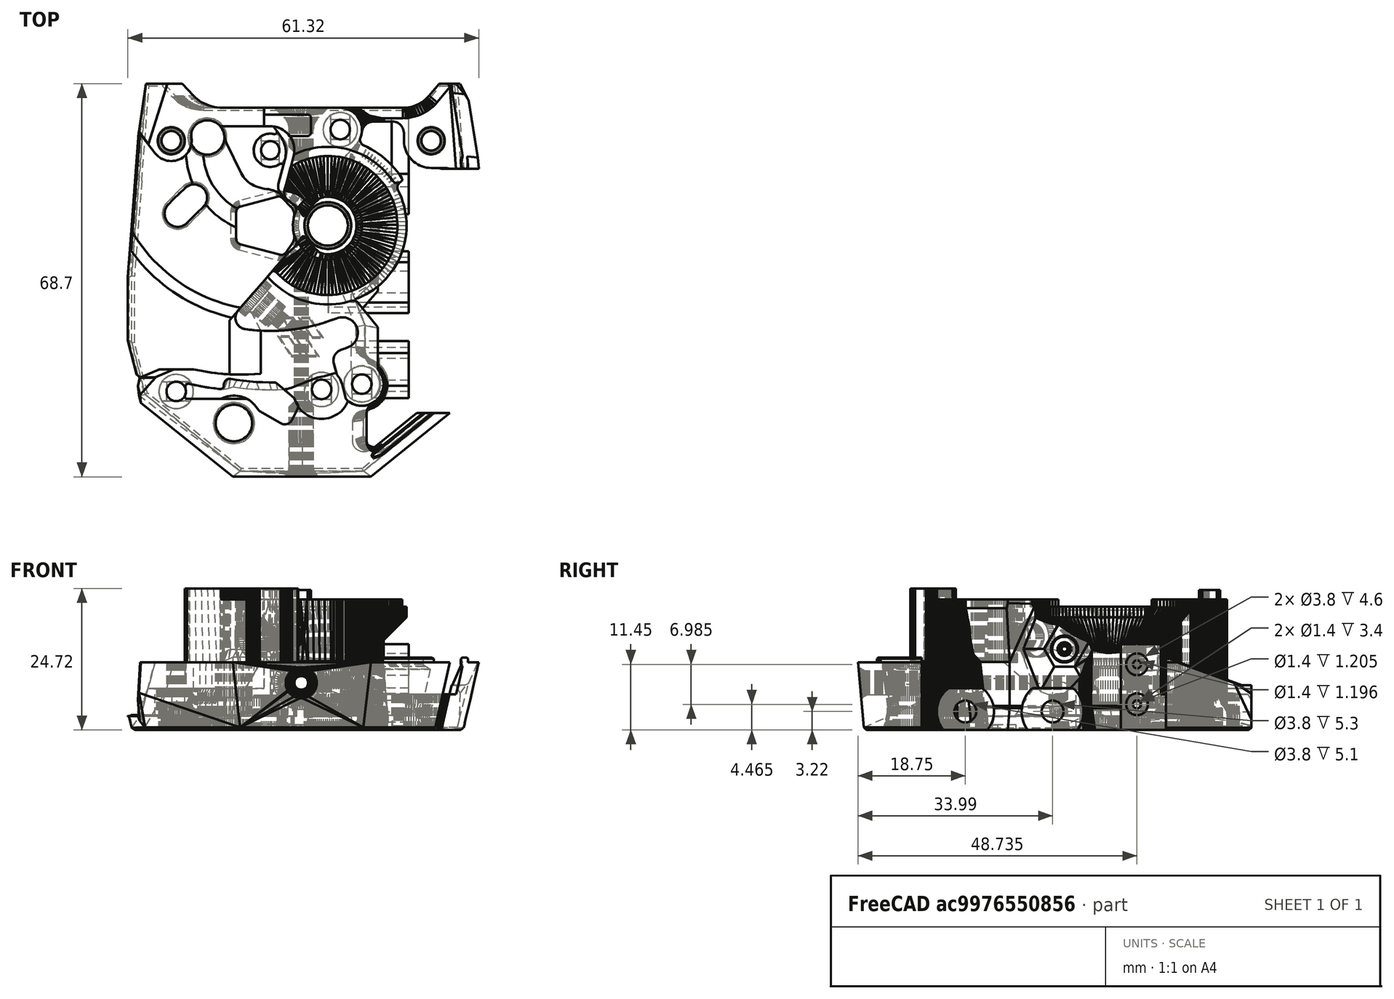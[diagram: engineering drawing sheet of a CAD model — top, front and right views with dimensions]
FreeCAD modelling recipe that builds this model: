
FCSTD DOCUMENT  (FreeCAD 0.19R24366 (Git))
Label: sb-mod2
License: All rights reserved
LicenseURL: http://en.wikipedia.org/wiki/All_rights_reserved
objects: Part::Cylinder×17, Part::Box×6, Part::MultiFuse×5, Part::Cut×3, Mesh::Feature×1, Part::Feature×1, Part::Compound×1
note: 33 computed .brp shape members not serialized (recipe doc carries the construction recipe); baked Part::Feature solids carry a one-line shape summary decoded from their .brp

FEATURE [Mesh::Feature] motor_plate
  Placement = pos=(-1.79,11.67,30.614) rot=(0,1,0;3.14159rad)
FEATURE [Part::Cylinder] Cylinder002
  Angle = 360
  AttacherType = Attacher::AttachEngine3D
  Height = 12
  Placement = pos=(9.55,-17.66,-3) rot=(0,0,1;0rad)
  Radius = 3.2
FEATURE [Part::Cylinder] Cylinder003
  Angle = 360
  AttacherType = Attacher::AttachEngine3D
  Height = 14
  Placement = pos=(17.64,0.14,3.22) rot=(0,-1,0;1.5708rad)
  Radius = 5.4
FEATURE [Part::Box] Box001  label="Cube001"
  AttacherType = Attacher::AttachEngine3D
  Height = 15
  Length = 10.6
  Placement = pos=(7.04,12.06,0) rot=(0,0,1;0rad)
  Width = 7
FEATURE [Part::Cylinder] Cylinder004
  Angle = 360
  AttacherType = Attacher::AttachEngine3D
  Height = 11.5
  Placement = pos=(3.62,10.05,0) rot=(0,0,1;0rad)
  Radius = 5.8
FEATURE [Part::Cylinder] Cylinder005
  Angle = 360
  AttacherType = Attacher::AttachEngine3D
  Height = 5
  Placement = pos=(3.62,10.05,11) rot=(0,0,1;0rad)
  Radius = 7
FEATURE [Part::Box] Box002  label="Cube002"
  AttacherType = Attacher::AttachEngine3D
  Height = 10
  Length = 10
  Placement = pos=(7.64,-21.3,7.32) rot=(0,0,1;0rad)
  Width = 30
FEATURE [Part::Box] Box003  label="Cube003"
  AttacherType = Attacher::AttachEngine3D
  Height = 10
  Length = 15
  Placement = pos=(2.64,-21.3,-9.985) rot=(0,0,1;0rad)
  Width = 30
FEATURE [Part::Cylinder] Cylinder001
  Angle = 360
  AttacherType = Attacher::AttachEngine3D
  Height = 10
  Placement = pos=(17.64,-15.1,3.22) rot=(0,-1,0;1.5708rad)
  Radius = 5
FEATURE [Part::Cylinder] Cylinder006
  Angle = 360
  AttacherType = Attacher::AttachEngine3D
  Height = 4.6
  Placement = pos=(17.64,14.885,4.465) rot=(0,-1,0;1.5708rad)
  Radius = 1.9
FEATURE [Part::Cylinder] Cylinder007
  Angle = 360
  AttacherType = Attacher::AttachEngine3D
  Height = 4.6
  Placement = pos=(17.64,14.885,11.45) rot=(0,-1,0;1.5708rad)
  Radius = 1.9
FEATURE [Part::Cylinder] Cylinder008
  Angle = 360
  AttacherType = Attacher::AttachEngine3D
  Height = 5.3
  Placement = pos=(17.64,0.14,3.22) rot=(0,-1,0;1.5708rad)
  Radius = 1.9
FEATURE [Part::Box] Box004  label="Cube004"
  AttacherType = Attacher::AttachEngine3D
  Height = 13
  Length = 14
  Placement = pos=(17.64,-22.73,0) rot=(0,0,1;0rad)
  Width = 42.7
FEATURE [Part::Feature] main_body001_solid  label="main_body001 (Solid)"
  shape: bbox 62.85 x 68.69 x 24.7 mm, 21214 faces (baked)
FEATURE [Part::Cylinder] Cylinder009
  Angle = 360
  AttacherType = Attacher::AttachEngine3D
  Height = 8
  Placement = pos=(17.64,14.885,4.465) rot=(0,-1,0;1.5708rad)
  Radius = 0.7
FEATURE [Part::Cylinder] Cylinder010
  Angle = 360
  AttacherType = Attacher::AttachEngine3D
  Height = 8
  Placement = pos=(17.64,14.885,11.45) rot=(0,-1,0;1.5708rad)
  Radius = 0.7
FEATURE [Part::Cylinder] Cylinder
  Angle = 360
  AttacherType = Attacher::AttachEngine3D
  Height = 5.1
  Placement = pos=(17.64,-15.1,3.22) rot=(0,-1,0;1.5708rad)
  Radius = 1.9
FEATURE [Part::MultiFuse] Fusion003
  Shapes = -> [Cylinder,Cylinder006,Cylinder007,Cylinder008,Box004,Cylinder009,Cylinder010]
FEATURE [Part::MultiFuse] Fusion004
  Shapes = -> [Box003,Cylinder002,Cylinder004,Cylinder005,Box002]
FEATURE [Part::MultiFuse] Fusion
  Shapes = -> [Cylinder003,Box001,Cylinder001]
FEATURE [Part::Cut] Cut
  Base = -> Fusion
  Tool = -> Fusion004
FEATURE [Part::Cylinder] Cylinder011
  Angle = 360
  AttacherType = Attacher::AttachEngine3D
  Height = 5.1
  Placement = pos=(17.64,-15.1,3.22) rot=(0,-1,0;1.5708rad)
  Radius = 1.9
FEATURE [Part::Cylinder] Cylinder012
  Angle = 360
  AttacherType = Attacher::AttachEngine3D
  Height = 4.6
  Placement = pos=(17.64,14.885,4.465) rot=(0,-1,0;1.5708rad)
  Radius = 1.9
FEATURE [Part::Cylinder] Cylinder013
  Angle = 360
  AttacherType = Attacher::AttachEngine3D
  Height = 4.6
  Placement = pos=(17.64,14.885,11.45) rot=(0,-1,0;1.5708rad)
  Radius = 1.9
FEATURE [Part::Cylinder] Cylinder014
  Angle = 360
  AttacherType = Attacher::AttachEngine3D
  Height = 5.3
  Placement = pos=(17.64,0.14,3.22) rot=(0,-1,0;1.5708rad)
  Radius = 1.9
FEATURE [Part::Box] Box005  label="Cube005"
  AttacherType = Attacher::AttachEngine3D
  Height = 13
  Length = 14
  Placement = pos=(17.64,-22.73,0) rot=(0,0,1;0rad)
  Width = 42.7
FEATURE [Part::Cylinder] Cylinder015
  Angle = 360
  AttacherType = Attacher::AttachEngine3D
  Height = 8
  Placement = pos=(17.64,14.885,4.465) rot=(0,-1,0;1.5708rad)
  Radius = 0.7
FEATURE [Part::Cylinder] Cylinder016
  Angle = 360
  AttacherType = Attacher::AttachEngine3D
  Height = 8
  Placement = pos=(17.64,14.885,11.45) rot=(0,-1,0;1.5708rad)
  Radius = 0.7
FEATURE [Part::MultiFuse] Fusion005
  Shapes = -> [Cylinder011,Cylinder012,Cylinder013,Cylinder014,Box005,Cylinder015,Cylinder016]
FEATURE [Part::Cut] Cut001
  Base = -> Cut
  Tool = -> Fusion005
FEATURE [Part::Cut] Cut002
  Base = -> main_body001_solid
  Tool = -> Fusion003
FEATURE [Part::Box] Box  label="Cube"
  AttacherType = Attacher::AttachEngine3D
  Height = 6.2
  Length = 3
  Placement = pos=(14.64,18,0) rot=(0,0,1;0rad)
  Width = 10.7
FEATURE [Part::MultiFuse] Fusion006
  Shapes = -> [Cut001,Box]
FEATURE [Part::Compound] Compound
  Links = -> [Cut002,Fusion006]
